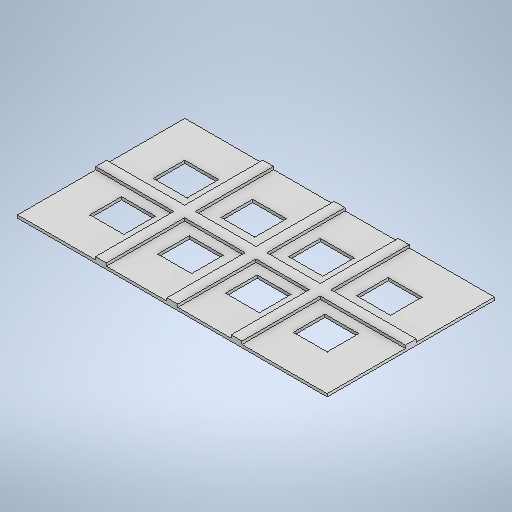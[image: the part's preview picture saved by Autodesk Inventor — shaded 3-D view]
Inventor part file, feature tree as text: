
AUTODESK INVENTOR PART (.ipt)
format: ipt  version: 2025 (Build 290162000, 162)  size: 347,136 bytes
history: native  units: in
note: dims shown in document units (in); Inventor stores cm internally (conversion verified against a paired STEP export)
features: sketch x3, extrude x2, projected_geometry x1
ambient origin geometry x8: Origin, YZ Plane, XZ Plane, XY Plane, X Axis, Y Axis, Z Axis, Center Point
bodies: Solid1 (feature_tree)
feature tree (6):
  extrude  "Extrusion1"  Depth=0.9375in
  extrude  "Extrusion2"  Depth=1.875in
  sketch  "Sketch1"  dims[d1=1.0in d2=0.9375in]
  sketch  "Sketch Rectangular Pattern1"  dims[d3=0.875in d4=1.5748in d6=1.875in d7=0.7874in d9=1.75in]
  sketch  "Sketch2"  dims[d12=1.0in d13=1.0in d14=0.0787in d15=0.0in d16=0.3in d17=0.3in d18=0.3in d19=0.3in d20=0.0787in d21=0.0in]
  projected_geometry  "Projected Loop1"
